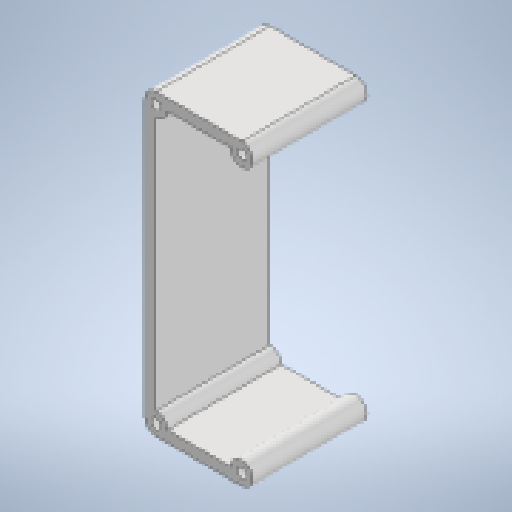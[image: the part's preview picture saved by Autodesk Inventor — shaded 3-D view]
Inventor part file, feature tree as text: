
AUTODESK INVENTOR PART (.ipt)
format: ipt  version: 2025.1 (Build 291241000, 241)  size: 155,648 bytes
history: native  units: mm
features: other x4, reference x4, sketch x1, extrude x1
ambient origin geometry x8: Origin, YZ Plane, XZ Plane, XY Plane, X Axis, Y Axis, Z Axis, Center Point
bodies: Body1 (feature_tree)
feature tree (10):
  other  "ソリッド1"
  sketch  "スケッチ1"
  other  "作業平面1"
  extrude  "押し出し1"  Depth=2.6mm
  reference  "参照1"
  reference  "参照2"
  reference  "参照3"
  reference  "参照4"
  other  "Assembly1"
  other  "kataue:1"
